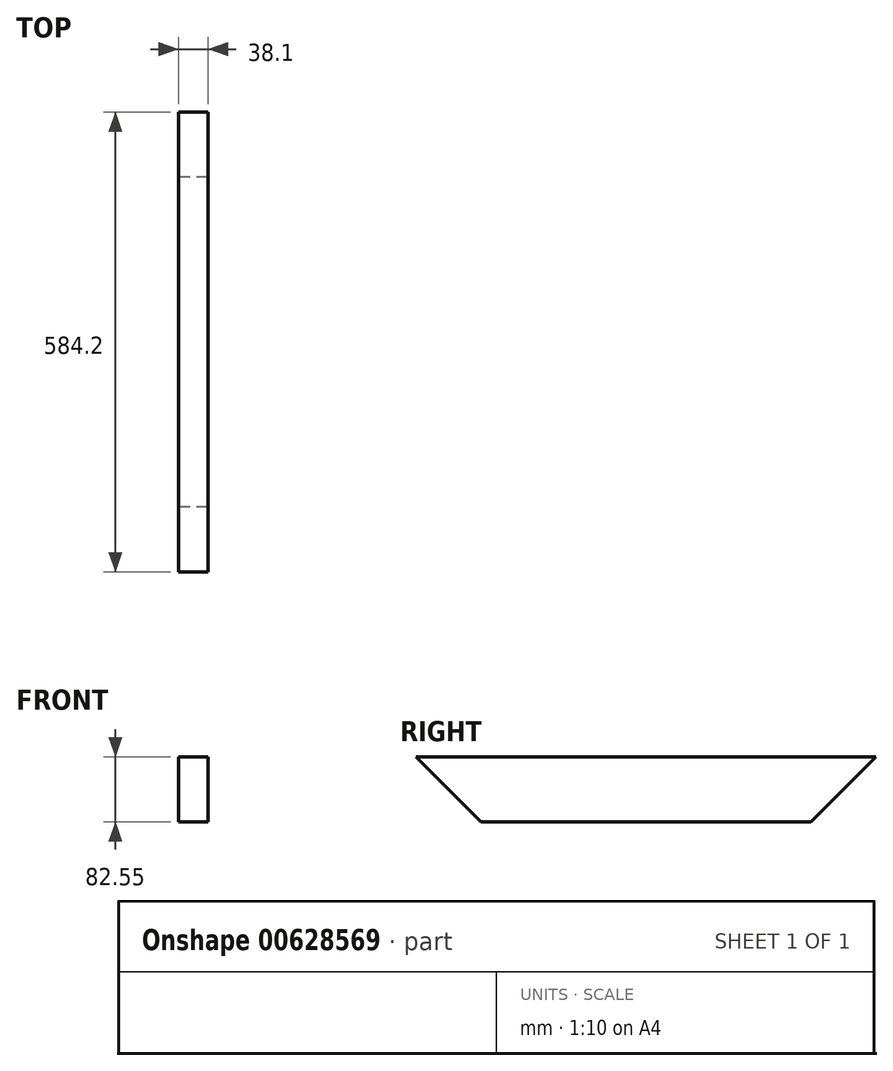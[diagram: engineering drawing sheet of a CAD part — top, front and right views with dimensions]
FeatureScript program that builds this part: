
annotation { "Feature Type Name" : "Feature", "Feature Type Description" : "" }
export const myFeature = defineFeature(function(context is Context, id is Id, definition is map)
    precondition{}
    {
        {
            var Q0;
            Q0=qCreatedBy(makeId("Right.planeOp"),FACE);
            var sketch = newSketch(context, id + "F0", { "sketchPlane" : qUnion([Q0])});
            skLineSegment(sketch, "E0.bottom", {"start": v(209.55, -82.55) * mm, "end": v(-209.55, -82.55) * mm});
            skLineSegment(sketch, "E0.top", {"start": v(292.1, 0) * mm, "end": v(-292.1, 0) * mm});
            skPoint(sketch, "E0.middle", {"position": v(0, 0) * mm});
            skLineSegment(sketch, "E1", {"start": v(-292.1, 0) * mm, "end": v(-209.55, -82.55) * mm});
            skLineSegment(sketch, "E2", {"start": v(292.1, 0) * mm, "end": v(209.55, -82.55) * mm});
            skSolve(sketch);
        }
        {
            var Q0;
            Q0 = qSketchRegion(id + "F0", true);
            extrude(context, id + "F1", {"entities" : qUnion([Q0]), "endBound" : BoundingType.SYMMETRIC, "depth" : 38.1 * mm, "offsetDistance" : 25.4 * mm});
        }
    });
